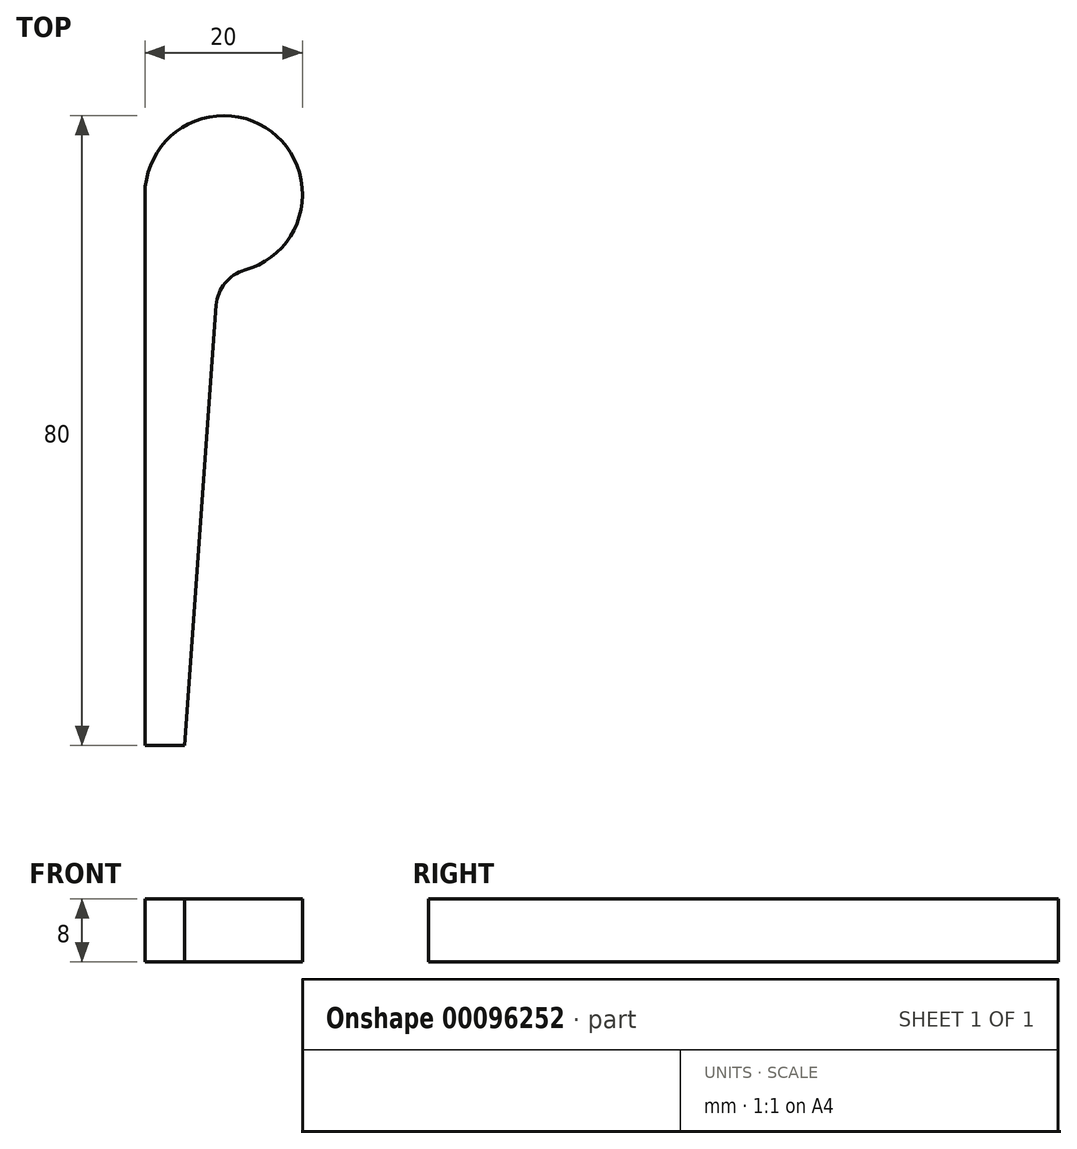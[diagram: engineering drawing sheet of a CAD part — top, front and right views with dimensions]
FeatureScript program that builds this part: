
annotation { "Feature Type Name" : "Feature", "Feature Type Description" : "" }
export const myFeature = defineFeature(function(context is Context, id is Id, definition is map)
    precondition{}
    {
        {
            var Q0;
            Q0=qCreatedBy(makeId("Top.planeOp"),FACE);
            var sketch = newSketch(context, id + "F0", { "sketchPlane" : qUnion([Q0])});
            skLineSegment(sketch, "E0.top", {"start": v(5, 35) * mm, "end": v(-5, 35) * mm, "construction": true});
            skLineSegment(sketch, "E0.right", {"start": v(-5, -35) * mm, "end": v(-5, 35) * mm});
            skPoint(sketch, "E0.middle", {"position": v(0, 0) * mm});
            skArc(sketch, "E1", {"start": v(-5, 35) * mm, "mid": v(11.05, 42.96) * mm, "end": v(7.68, 25.37) * mm});
            skArc(sketch, "E2.filletArc", {"start": v(7.68, 25.37) * mm, "mid": v(5.16, 23.72) * mm, "end": v(4.04, 20.91) * mm});
            skLineSegment(sketch, "E3", {"start": v(4.04, 20.91) * mm, "end": v(0, -35) * mm});
            skLineSegment(sketch, "E4", {"start": v(-5, -35) * mm, "end": v(0, -35) * mm});
            skSolve(sketch);
        }
        {
            var Q0;
            Q0=makeQuery(id+"F0.imprint","IMPRINT",FACE,{"disambiguationData":[TD([[makeQuery(id+"F0.imprint","IMPRINT",EDGE,{"derivedFrom":sQuery(id+"F0.wireOp",EDGE,"E0.right")}),-1.0]])]});
            extrude(context, id + "F1", {"entities" : qUnion([Q0]), "depth" : 8 * mm});
        }
    });
